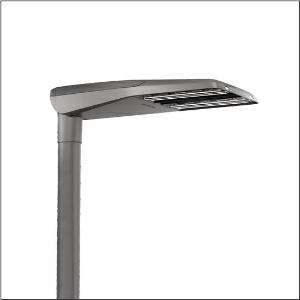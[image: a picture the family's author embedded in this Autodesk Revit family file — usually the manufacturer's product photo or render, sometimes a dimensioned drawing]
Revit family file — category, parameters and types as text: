
# Revit family: streetlight_sl_11_iq_midi___st1_2p1_0_5xc3g51f08me_c537
name_source: partatom
category: Lighting Fixtures
units: mm (PartAtom-declared; Revit-internal decimal feet)

## family parameters
Cut with Voids When Loaded = No
Host = Face
Light Source = No
Part Type = Normal
Room Calculation Point = No
Round Connector Dimension = Use Diameter
Shared = No

## types (1)
- --- (1 x LED, 17750 lm, 121.7 W, 3000K)
    Apparent Load = 122 VA
    CIE Flux Codes = 31 68 95 100 100
    Color Rendering = 70
    Color Temperature = 3000K
    Default Elevation = 1800 mm
    Description = Streetlight SL 11 iQ midi, mast luminaire, primary light control with 3 zone facetted reflector, of plastic, silver coated, highly specular, primary optical cover: cover, of PMMA, transparent, light distribution: ST1.2P1.0, light emission: direct distribution, primary light characteristic: asymmetric, installation type: post-top, side-entry, LED, High Power LED, rated luminous flux: 17.750lm, luminous efficacy: 146lm/W, light colour: 730, colour temperature: 3000K, control: Street-Remote, optimised constant luminous flux control (CLO 2.0), Auto-Match, Desk-Remote (wireless, voltage-free reading and setting of iQ features in the workshop via application-optimized NFC function/RFID function), Light-Fading, Smart-Wire, Night-Set, Lumen-Switch, Temp-Guard, with cable H07RN-F 5x 1.5mm², mains connection: 230..240V, AC, 50/60Hz, connection cable pre-assembled, cable length: 12,5m, start of lifetime: 122W, end of service life: 129W, reduction: 56W, luminaire housing, of diecast aluminium, powder-coated, Siteco® metallic grey (DB 702S), please order mast flange separately, inclination adjustable without tools: 0°, 5°, 10°, 15° (post-top) | 0°, -5°, -10°, -15° (side-entry), sealing non-destructively replaceable, multi-level sealing system, length: 780mm, width: 376mm, height: 118mm, mast flange for spigot size: 42mm (side-entry): 5XC10008XM4, 60/48mm (side-entry/post-top): 5XC10108XM2, 76/60mm (side-entry/post-top): 5XC10108XM1, equipment: Power, protection rating (complete): IP66, insulation class (complete): insulation class II (safety insulation), certification: CE, ENEC, VDE, impact resistance: IK09, permissible operating ambient temperature for outdoor applications: -25..+50°C, standard-compliant lighting for roads and squares, Environmental Product Declaration (EPD) tested and certified by an independent institute, packaging unit: 1 piece

Light Distribution: ST1.2P1.0
    Height = 118 mm
    Lamp = 1 x LED
    Lamp Light Flux = 17750 lm
    Lamp Power = 121.7 W
    Lamp count = 1
    Length = 780 mm
    Luminous efficacy = 146 lm/W
    Manufacturer = Siteco
    ModVariant = No
    Model = 5XC3G51F08ME
    Number of Poles = 1
    OnlyDefault = Yes
    Power Factor = 1
    Product Name = Streetlight SL 11 iQ midi | ST1.2P1.0
    Product group = mast luminaire | pylon top
    ProductGroupID = 6100
    Protection Class = Protection class II
    Protection Degree = IP 66
    RLX_Detail_Level = 1
    RLX_Emergency_Light_Flux = 0 lm
    RLX_Emergency_Type = 0
    RLX_Emergency_Type_DB = No
    RlxData = <blob elided: 29725 chars, md5=c0155dd4>
    Socket = socket
    Standby Power = 0 W
    System Light Flux = 17750 lm
    System Power = 122 W
    Type Comments = factory setting: luminous flux: 100 % | dim-lin: 254 | 544 mA
    Type Image = l_1005960.jpg
    URL = http://relux.com
    VarID = @adj_004945
    Voltage = 0 V
    Weight = 0.00 kg
    Width = 376 mm

## geometry (parser evidence)
native form markers: Blend x4, Sweep x10
no freeform markers — native parametric forms only
